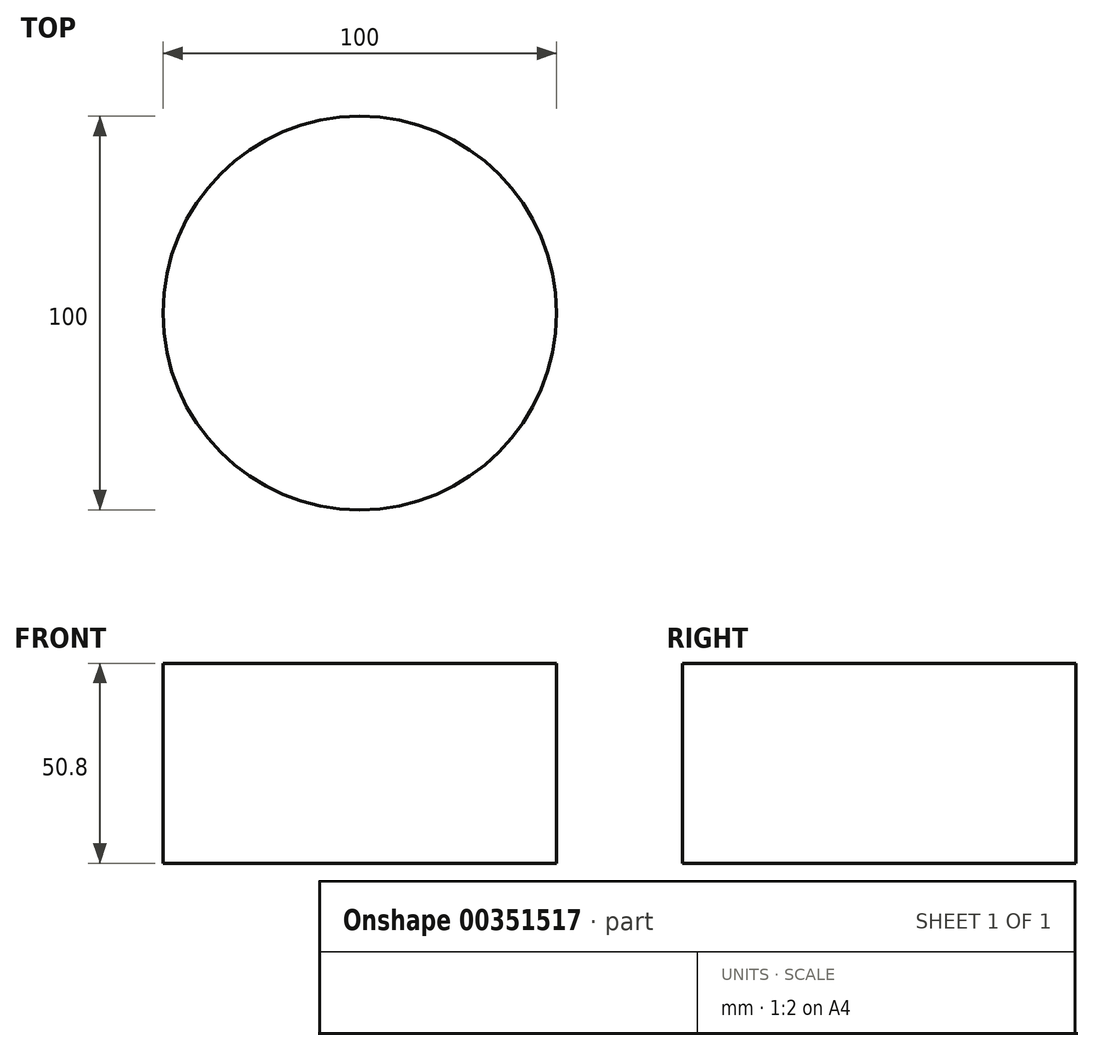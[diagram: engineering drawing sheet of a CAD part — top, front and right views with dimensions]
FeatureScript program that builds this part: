
annotation { "Feature Type Name" : "Feature", "Feature Type Description" : "" }
export const myFeature = defineFeature(function(context is Context, id is Id, definition is map)
    precondition{}
    {
        {
            var Q0;
            Q0=qCreatedBy(makeId("Top.planeOp"),FACE);
            var sketch = newSketch(context, id + "F0", { "sketchPlane" : qUnion([Q0])});
            skCircle(sketch, "E0", {"center": v(0, 0) * mm, "radius": 50 * mm});
            skSolve(sketch);
        }
        {
            var Q0;
            Q0=makeQuery(id+"F0.imprint","IMPRINT",FACE,{"disambiguationData":[TD([[makeQuery(id+"F0.imprint","IMPRINT",EDGE,{"derivedFrom":sQuery(id+"F0.wireOp",EDGE,"E0")}),1.0]])]});
            extrude(context, id + "F1", {"entities" : qUnion([Q0]), "depth" : 50.8 * mm});
        }
    });
